# Revit family: Table-Teknion-Zones_ZNTBR-R2013
name_source: partatom
category: Furniture
revit_build: Autodesk Revit 2013 (Build: 20130531_2115(x64)
units: mm (PartAtom-declared; Revit-internal decimal feet)

## types (3) — shared parameters
Assembly Code = E2020200
Depth = 36"
Manufacturer = Teknion
Manufacturer Fax = 416.661.4586
Part Number = ZNTBR
Product Documentation Link = http://www.teknion.com
Product Line = Zones
Product Page URL = http://www.teknion.com
Series = Zones
Sustainability Data = http://www.teknion.com
URL = www.teknion.com
Unit Weight URL = http://www.teknion.com
Warranty = http://www.teknion.com
Width = 36"

## per-type parameters (varying)
| type | Description | Height | Model |
| Task Height | Round Bistro Table, Task Height, 36"dia | 29" | ZNTBRT36 |
| Counter Height | Round Bistro Table, Counter Height, 36"dia | 36" | ZNTBRC36 |
| Bar Height | Round Bistro Table, Bar Height, 36"dia | 42" | ZNTBRB36 |

## geometry (parser evidence)
native form markers: Blend x57, Sweep x2
no freeform markers — native parametric forms only
